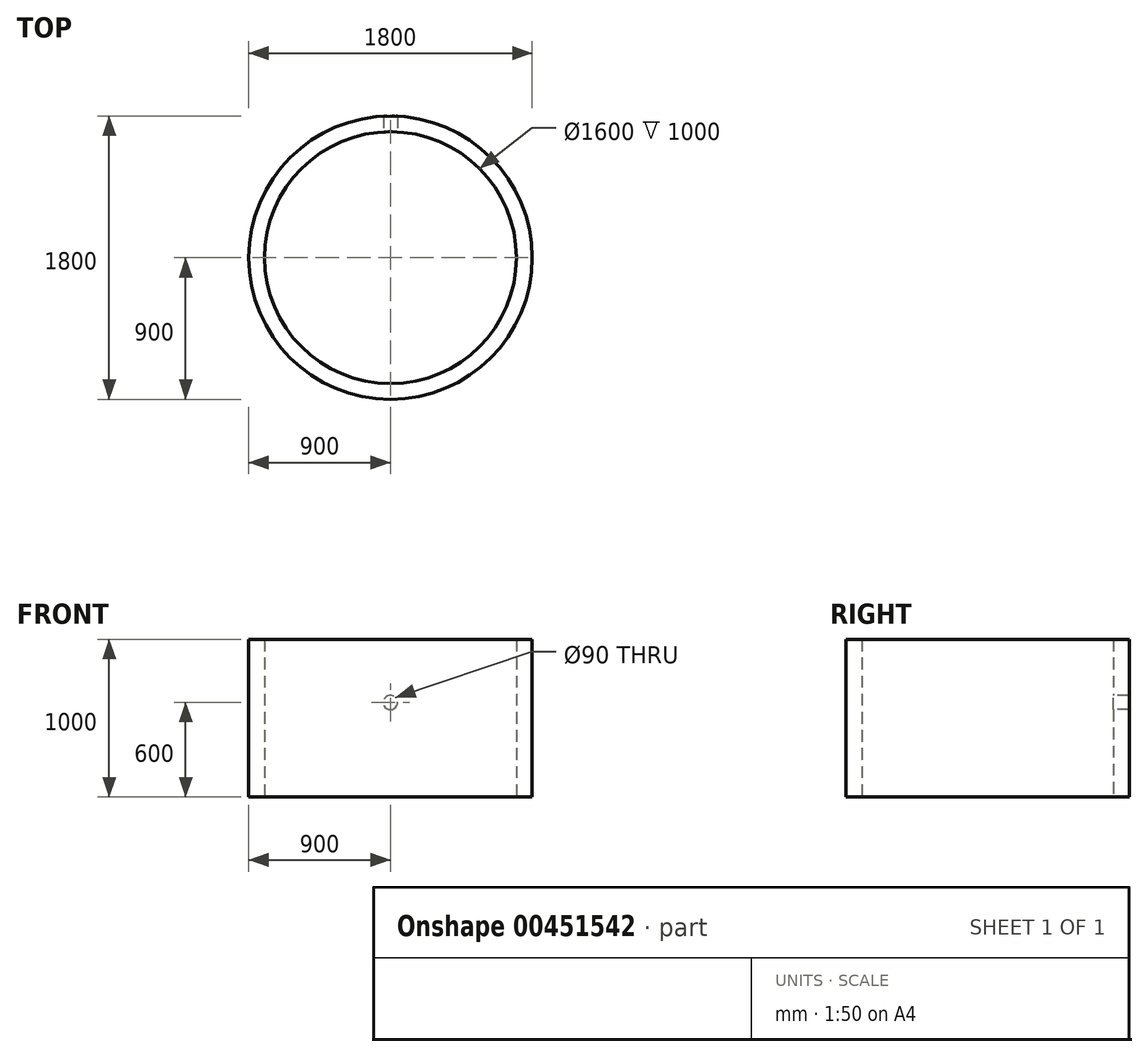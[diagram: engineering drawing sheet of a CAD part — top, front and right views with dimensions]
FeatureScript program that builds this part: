
annotation { "Feature Type Name" : "Feature", "Feature Type Description" : "" }
export const myFeature = defineFeature(function(context is Context, id is Id, definition is map)
    precondition{}
    {
        {
            var Q0;
            Q0=qCreatedBy(makeId("Top.planeOp"),FACE);
            var sketch = newSketch(context, id + "F0", { "sketchPlane" : qUnion([Q0])});
            skCircle(sketch, "E0", {"center": v(0, 0) * mm, "radius": 900 * mm});
            skCircle(sketch, "E1", {"center": v(0, 0) * mm, "radius": 800 * mm});
            skSolve(sketch);
        }
        {
            var Q0;
            Q0=makeQuery(id+"F0.imprint","IMPRINT",FACE,{"disambiguationData":[TD([[makeQuery(id+"F0.imprint","IMPRINT",EDGE,{"derivedFrom":sQuery(id+"F0.wireOp",EDGE,"E0")}),1.0]])]});
            extrude(context, id + "F1", {"entities" : qUnion([Q0]), "endBound" : BoundingType.SYMMETRIC, "depth" : 1000 * mm});
        }
        {
            var Q0;
            Q0=qCreatedBy(makeId("Front.planeOp"),FACE);
            var sketch = newSketch(context, id + "F2", { "sketchPlane" : qUnion([Q0])});
            skCircle(sketch, "E2", {"center": v(0, 100) * mm, "radius": 45 * mm});
            skSolve(sketch);
        }
        {
            var Q0;
            Q0=makeQuery(id+"F2.imprint","IMPRINT",FACE,{"disambiguationData":[TD([[makeQuery(id+"F2.imprint","IMPRINT",EDGE,{"derivedFrom":sQuery(id+"F2.wireOp",EDGE,"E2")}),1.0]])]});
            extrude(context, id + "F3", {"entities" : qUnion([Q0]), "operationType" : NewBodyOperationType.REMOVE, "oppositeDirection" : true, "depth" : 1000 * mm, "offsetDistance" : 25 * mm});
        }
    });
